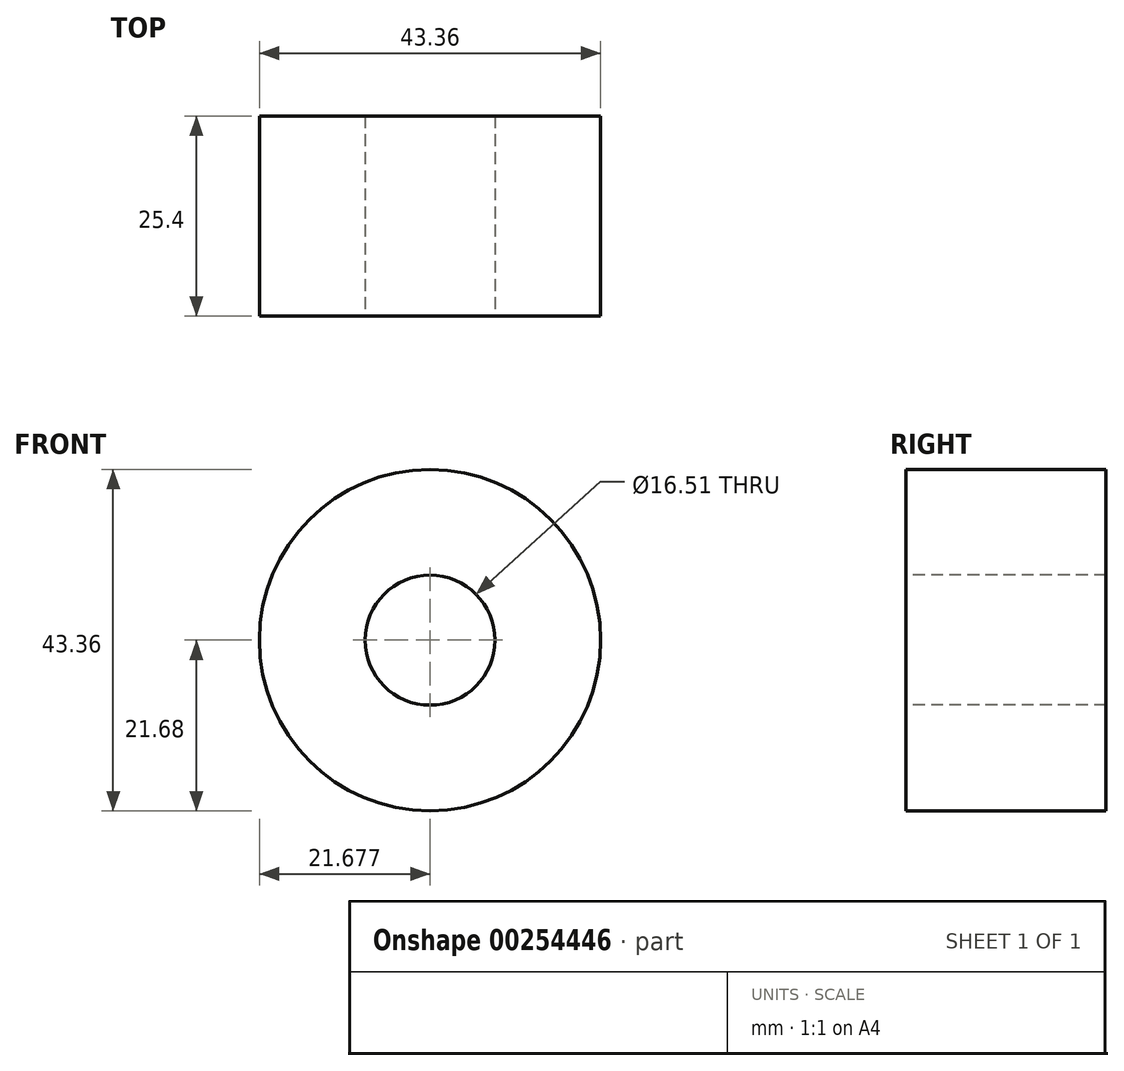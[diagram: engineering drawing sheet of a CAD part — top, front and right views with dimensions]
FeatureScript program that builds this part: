
annotation { "Feature Type Name" : "Feature", "Feature Type Description" : "" }
export const myFeature = defineFeature(function(context is Context, id is Id, definition is map)
    precondition{}
    {
        {
            var Q0;
            Q0=qCreatedBy(makeId("Front.planeOp"),FACE);
            var sketch = newSketch(context, id + "F0", { "sketchPlane" : qUnion([Q0])});
            skCircle(sketch, "E0", {"center": v(-16.22, 14.38) * mm, "radius": 21.68 * mm});
            skSolve(sketch);
        }
        {
            var Q0;
            Q0=makeQuery(id+"F0.imprint","IMPRINT",FACE,{"disambiguationData":[TD([[makeQuery(id+"F0.imprint","IMPRINT",EDGE,{"derivedFrom":sQuery(id+"F0.wireOp",EDGE,"E0")}),1.0]])]});
            extrude(context, id + "F1", {"entities" : qUnion([Q0]), "depth" : 25.4 * mm});
        }
        {
            var Q0;
            Q0=makeQuery(id+"F1.opExtrude","CAP_FACE",FACE,{"disambiguationData":[OSD([sQuery(id+"F0.wireOp",EDGE,"E0")])],"isStart":false});
            var sketch = newSketch(context, id + "F2", { "sketchPlane" : qUnion([Q0])});
            skPoint(sketch, "E1", {"position": v(-16.22, 14.38) * mm});
            skSolve(sketch);
        }
        {
            var Q0;
            Q0=sQuery(id+"F2.wireOp",VERTEX,"E1");
            var Q1;
            Q1=makeQuery(id+"F1.opExtrude","SWEPT_BODY",BODY,{"disambiguationData":[OSD([sQuery(id+"F0.wireOp",EDGE,"E0")])]});
            hole(context, id + "F3", {"style" : HoleStyle.SIMPLE, "endStyle" : HoleEndStyle.THROUGH, "holeDiameter" : 16.5 * mm, "tappedDepth" : 12.7 * mm, "tapClearance" : 3, "locations" : qUnion([Q0]), "scope" : qUnion([Q1])});
        }
    });
